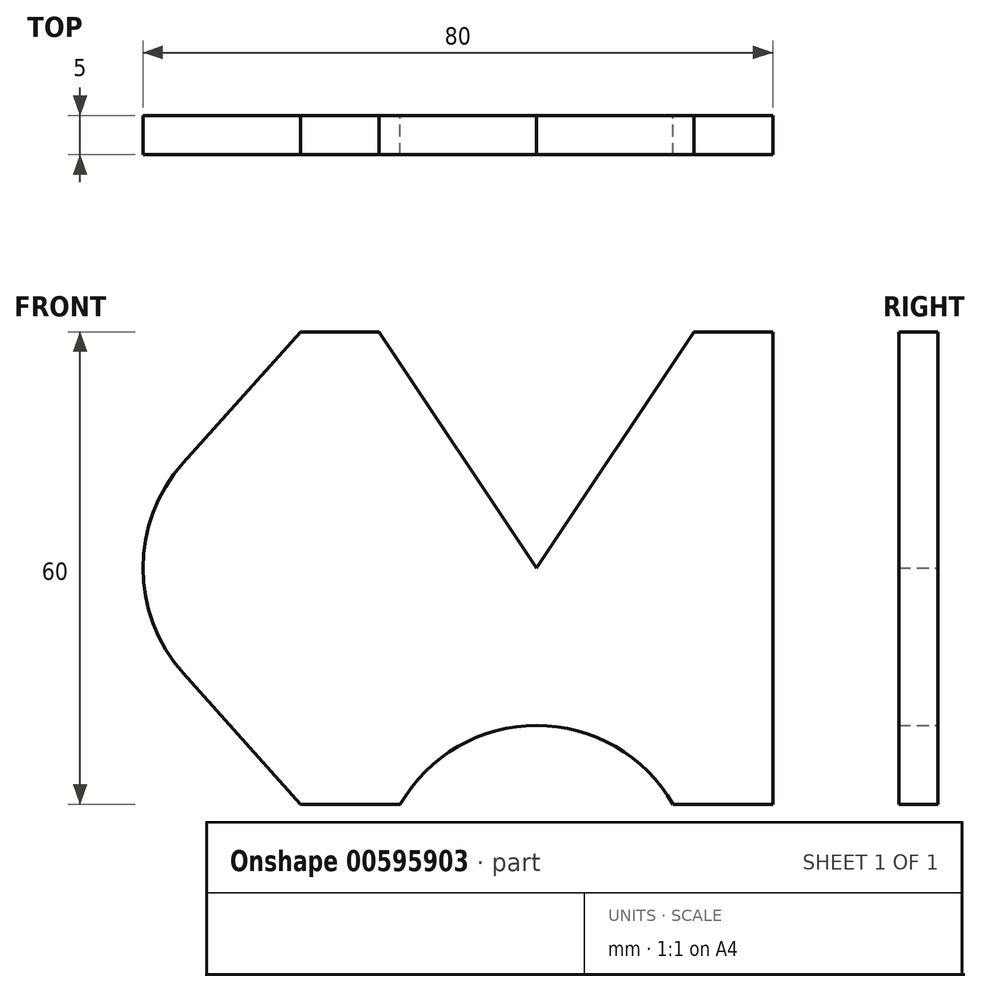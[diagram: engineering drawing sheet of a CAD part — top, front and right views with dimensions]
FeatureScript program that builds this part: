
annotation { "Feature Type Name" : "Feature", "Feature Type Description" : "" }
export const myFeature = defineFeature(function(context is Context, id is Id, definition is map)
    precondition{}
    {
        {
            var Q0;
            Q0=qCreatedBy(makeId("Front.planeOp"),FACE);
            var sketch = newSketch(context, id + "F0", { "sketchPlane" : qUnion([Q0])});
            skLineSegment(sketch, "E0", {"start": v(0, 0) * mm, "end": v(20, 30) * mm});
            skLineSegment(sketch, "E1", {"start": v(20, 30) * mm, "end": v(30, 30) * mm});
            skLineSegment(sketch, "E2", {"start": v(30, 30) * mm, "end": v(30, -30) * mm});
            skLineSegment(sketch, "E3", {"start": v(30, -30) * mm, "end": v(17.32, -30) * mm});
            skArc(sketch, "E4", {"start": v(17.32, -30) * mm, "mid": v(0, -20) * mm, "end": v(-17.32, -30) * mm});
            skLineSegment(sketch, "E5", {"start": v(-17.32, -30) * mm, "end": v(-30, -30) * mm});
            skLineSegment(sketch, "E6", {"start": v(-30, -30) * mm, "end": v(-44.9, -13.33) * mm});
            skArc(sketch, "E7", {"start": v(-44.9, 13.33) * mm, "mid": v(-50, 0) * mm, "end": v(-44.9, -13.33) * mm});
            skLineSegment(sketch, "E8", {"start": v(-44.9, 13.33) * mm, "end": v(-30, 30) * mm});
            skLineSegment(sketch, "E9", {"start": v(-30, 30) * mm, "end": v(-20, 30) * mm});
            skLineSegment(sketch, "E10", {"start": v(-20, 30) * mm, "end": v(0, 0) * mm});
            skSolve(sketch);
        }
        {
            var Q0;
            Q0=makeQuery(id+"F0.imprint","IMPRINT",FACE,{"disambiguationData":[TD([[makeQuery(id+"F0.imprint","IMPRINT",EDGE,{"derivedFrom":sQuery(id+"F0.wireOp",EDGE,"E0")}),-1.0]])]});
            extrude(context, id + "F1", {"entities" : qUnion([Q0]), "depth" : 5 * mm, "offsetDistance" : 25 * mm});
        }
    });
